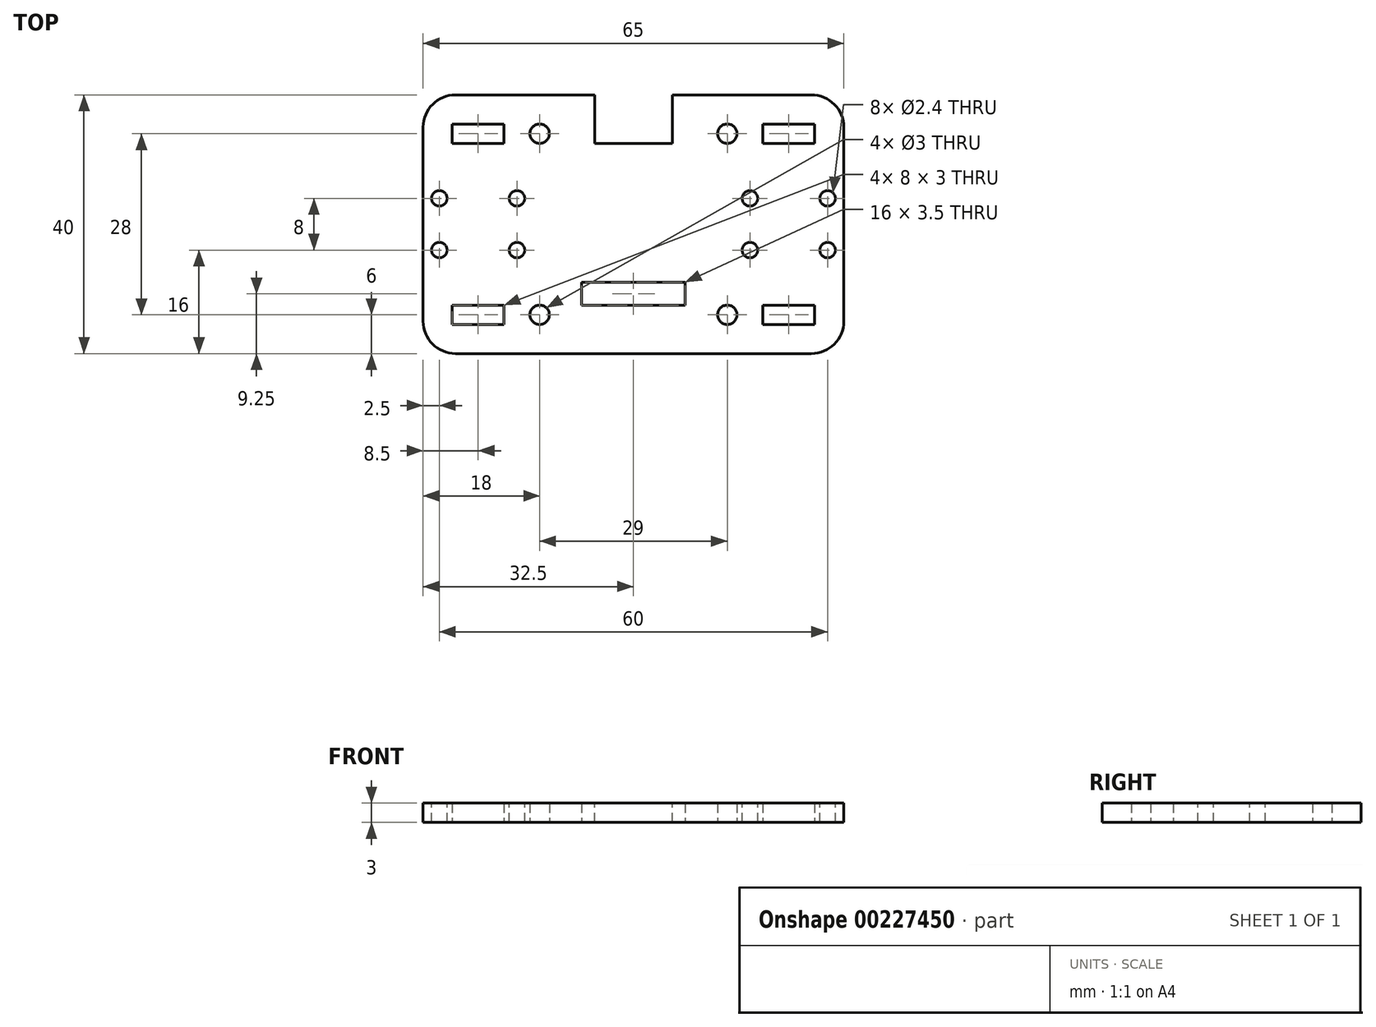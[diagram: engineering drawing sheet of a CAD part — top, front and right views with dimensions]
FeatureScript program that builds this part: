
annotation { "Feature Type Name" : "Feature", "Feature Type Description" : "" }
export const myFeature = defineFeature(function(context is Context, id is Id, definition is map)
    precondition{}
    {
        {
            assignVariable(context, id + "F0", {"name" : "Thickness", "anyValue" : 3});
        }
        {
            var Q0;
            Q0=qCreatedBy(makeId("Top.planeOp"),FACE);
            var sketch = newSketch(context, id + "F1", { "sketchPlane" : qUnion([Q0])});
            skLineSegment(sketch, "E0.bottom", {"start": v(32.5, -20) * mm, "end": v(-32.5, -20) * mm});
            skLineSegment(sketch, "E0.top", {"start": v(32.5, 20) * mm, "end": v(-32.5, 20) * mm});
            skLineSegment(sketch, "E0.left", {"start": v(32.5, -20) * mm, "end": v(32.5, 20) * mm});
            skLineSegment(sketch, "E0.right", {"start": v(-32.5, -20) * mm, "end": v(-32.5, 20) * mm});
            skPoint(sketch, "E0.middle", {"position": v(0, 0) * mm});
            skLineSegment(sketch, "E1", {"start": v(-32.5, -14) * mm, "end": v(32.5, -14) * mm, "construction": true});
            skPoint(sketch, "E2", {"position": v(-24, -14) * mm});
            skLineSegment(sketch, "E3.bottom", {"start": v(-20, -15.5) * mm, "end": v(-28, -15.5) * mm});
            skLineSegment(sketch, "E3.top", {"start": v(-20, -12.5) * mm, "end": v(-28, -12.5) * mm});
            skLineSegment(sketch, "E3.left", {"start": v(-20, -15.5) * mm, "end": v(-20, -12.5) * mm});
            skLineSegment(sketch, "E3.right", {"start": v(-28, -15.5) * mm, "end": v(-28, -12.5) * mm});
            skPoint(sketch, "E4.MirrorP", {"position": v(24, -14) * mm});
            skLineSegment(sketch, "E5.MirrorCS", {"start": v(28, -15.5) * mm, "end": v(28, -12.5) * mm});
            skLineSegment(sketch, "E6.MirrorCS", {"start": v(20, -15.5) * mm, "end": v(20, -12.5) * mm});
            skLineSegment(sketch, "E7.MirrorCS", {"start": v(20, -12.5) * mm, "end": v(28, -12.5) * mm});
            skLineSegment(sketch, "E8.MirrorCS", {"start": v(20, -15.5) * mm, "end": v(28, -15.5) * mm});
            skPoint(sketch, "E9.MirrorP", {"position": v(24, 14) * mm});
            skPoint(sketch, "E10.MirrorP", {"position": v(-24, 14) * mm});
            skLineSegment(sketch, "E11.MirrorCS", {"start": v(-20, 12.5) * mm, "end": v(-28, 12.5) * mm});
            skLineSegment(sketch, "E12.MirrorCS", {"start": v(-20, 15.5) * mm, "end": v(-20, 12.5) * mm});
            skLineSegment(sketch, "E13.MirrorCS", {"start": v(-28, 15.5) * mm, "end": v(-28, 12.5) * mm});
            skLineSegment(sketch, "E14.MirrorCS", {"start": v(28, 15.5) * mm, "end": v(28, 12.5) * mm});
            skLineSegment(sketch, "E15.MirrorCS", {"start": v(-20, 15.5) * mm, "end": v(-28, 15.5) * mm});
            skLineSegment(sketch, "E16.MirrorCS", {"start": v(20, 15.5) * mm, "end": v(28, 15.5) * mm});
            skLineSegment(sketch, "E17.MirrorCS", {"start": v(20, 15.5) * mm, "end": v(20, 12.5) * mm});
            skLineSegment(sketch, "E18.MirrorCS", {"start": v(20, 12.5) * mm, "end": v(28, 12.5) * mm});
            skCircle(sketch, "E19", {"center": v(-14.5, -14) * mm, "radius": 1.5 * mm});
            skCircle(sketch, "E20.MirrorC", {"center": v(14.5, -14) * mm, "radius": 1.5 * mm});
            skCircle(sketch, "E21.MirrorC", {"center": v(-14.5, 14) * mm, "radius": 1.5 * mm});
            skCircle(sketch, "E22.MirrorC", {"center": v(14.5, 14) * mm, "radius": 1.5 * mm});
            skLineSegment(sketch, "E23.bottom", {"start": v(-8, -12.5) * mm, "end": v(8, -12.5) * mm});
            skLineSegment(sketch, "E23.top", {"start": v(-8, -9) * mm, "end": v(8, -9) * mm});
            skLineSegment(sketch, "E23.left", {"start": v(-8, -12.5) * mm, "end": v(-8, -9) * mm});
            skLineSegment(sketch, "E23.right", {"start": v(8, -12.5) * mm, "end": v(8, -9) * mm});
            skPoint(sketch, "E24", {"position": v(0, -9) * mm});
            skSolve(sketch);
        }
        {
            var Q0;
            Q0=makeQuery(id+"F1.imprint","IMPRINT",FACE,{"disambiguationData":[TD([[makeQuery(id+"F1.imprint","IMPRINT",EDGE,{"derivedFrom":sQuery(id+"F1.wireOp",EDGE,"E0.bottom")}),-1.0]])]});
            extrude(context, id + "F2", {"entities" : qUnion([Q0]), "depth" : (getVariable(context, 'Thickness')) * mm});
        }
        {
            var Q0;
            Q0=makeQuery(id+"F2.opExtrude","CAP_FACE",FACE,{"disambiguationData":[OSD([sQuery(id+"F1.wireOp",EDGE,"E0.bottom"),sQuery(id+"F1.wireOp",EDGE,"E0.top"),sQuery(id+"F1.wireOp",EDGE,"E0.left"),sQuery(id+"F1.wireOp",EDGE,"E0.right"),sQuery(id+"F1.wireOp",EDGE,"E3.bottom"),sQuery(id+"F1.wireOp",EDGE,"E3.top"),sQuery(id+"F1.wireOp",EDGE,"E3.left"),sQuery(id+"F1.wireOp",EDGE,"E3.right"),sQuery(id+"F1.wireOp",EDGE,"E5.MirrorCS"),sQuery(id+"F1.wireOp",EDGE,"E6.MirrorCS"),sQuery(id+"F1.wireOp",EDGE,"E7.MirrorCS"),sQuery(id+"F1.wireOp",EDGE,"E8.MirrorCS"),sQuery(id+"F1.wireOp",EDGE,"E11.MirrorCS"),sQuery(id+"F1.wireOp",EDGE,"E12.MirrorCS"),sQuery(id+"F1.wireOp",EDGE,"E13.MirrorCS"),sQuery(id+"F1.wireOp",EDGE,"E14.MirrorCS"),sQuery(id+"F1.wireOp",EDGE,"E15.MirrorCS"),sQuery(id+"F1.wireOp",EDGE,"E16.MirrorCS"),sQuery(id+"F1.wireOp",EDGE,"E17.MirrorCS"),sQuery(id+"F1.wireOp",EDGE,"E18.MirrorCS"),sQuery(id+"F1.wireOp",EDGE,"E19"),sQuery(id+"F1.wireOp",EDGE,"E20.MirrorC"),sQuery(id+"F1.wireOp",EDGE,"E21.MirrorC"),sQuery(id+"F1.wireOp",EDGE,"E22.MirrorC")])],"isStart":false});
            var sketch = newSketch(context, id + "F3", { "sketchPlane" : qUnion([Q0])});
            skPoint(sketch, "E25", {"position": v(-30, 4) * mm});
            skPoint(sketch, "E26.0.1.0", {"position": v(-30, -4) * mm});
            skPoint(sketch, "E26.1.0.0", {"position": v(-18, 4) * mm});
            skPoint(sketch, "E26.1.1.0", {"position": v(-18, -4) * mm});
            skLineSegment(sketch, "E26.direction1", {"start": v(-30, 4) * mm, "end": v(-18, 4) * mm, "construction": true});
            skLineSegment(sketch, "E26.direction2", {"start": v(-30, 4) * mm, "end": v(-30, -4) * mm, "construction": true});
            skPoint(sketch, "E27.MirrorP", {"position": v(18, -4) * mm});
            skLineSegment(sketch, "E28.MirrorCS", {"start": v(30, 4) * mm, "end": v(18, 4) * mm, "construction": true});
            skLineSegment(sketch, "E29.MirrorCS", {"start": v(30, 4) * mm, "end": v(30, -4) * mm, "construction": true});
            skPoint(sketch, "E30.MirrorP", {"position": v(18, 4) * mm});
            skSolve(sketch);
        }
        {
            var Q0;
            Q0=sQuery(id+"F3.wireOp",VERTEX,"E25");
            var Q1;
            Q1=sQuery(id+"F3.wireOp",VERTEX,"E26.0.1.0");
            var Q2;
            Q2=sQuery(id+"F3.wireOp",VERTEX,"E26.1.0.0");
            var Q3;
            Q3=sQuery(id+"F3.wireOp",VERTEX,"E26.1.1.0");
            var Q4;
            Q4=sQuery(id+"F3.wireOp",VERTEX,"E30.MirrorP");
            var Q5;
            Q5=sQuery(id+"F3.wireOp",VERTEX,"E27.MirrorP");
            var Q6;
            Q6=sQuery(id+"F3.wireOp",VERTEX,"E29.MirrorCS.start");
            var Q7;
            Q7=sQuery(id+"F3.wireOp",VERTEX,"E29.MirrorCS.end");
            var Q8;
            Q8=makeQuery(id+"F2.opExtrude","SWEPT_BODY",BODY,{"disambiguationData":[OSD([sQuery(id+"F1.wireOp",EDGE,"E0.bottom"),sQuery(id+"F1.wireOp",EDGE,"E0.top"),sQuery(id+"F1.wireOp",EDGE,"E0.left"),sQuery(id+"F1.wireOp",EDGE,"E0.right"),sQuery(id+"F1.wireOp",EDGE,"E3.bottom"),sQuery(id+"F1.wireOp",EDGE,"E3.top"),sQuery(id+"F1.wireOp",EDGE,"E3.left"),sQuery(id+"F1.wireOp",EDGE,"E3.right"),sQuery(id+"F1.wireOp",EDGE,"E5.MirrorCS"),sQuery(id+"F1.wireOp",EDGE,"E6.MirrorCS"),sQuery(id+"F1.wireOp",EDGE,"E7.MirrorCS"),sQuery(id+"F1.wireOp",EDGE,"E8.MirrorCS"),sQuery(id+"F1.wireOp",EDGE,"E11.MirrorCS"),sQuery(id+"F1.wireOp",EDGE,"E12.MirrorCS"),sQuery(id+"F1.wireOp",EDGE,"E13.MirrorCS"),sQuery(id+"F1.wireOp",EDGE,"E14.MirrorCS"),sQuery(id+"F1.wireOp",EDGE,"E15.MirrorCS"),sQuery(id+"F1.wireOp",EDGE,"E16.MirrorCS"),sQuery(id+"F1.wireOp",EDGE,"E17.MirrorCS"),sQuery(id+"F1.wireOp",EDGE,"E18.MirrorCS"),sQuery(id+"F1.wireOp",EDGE,"E19"),sQuery(id+"F1.wireOp",EDGE,"E20.MirrorC"),sQuery(id+"F1.wireOp",EDGE,"E21.MirrorC"),sQuery(id+"F1.wireOp",EDGE,"E22.MirrorC")])]});
            hole(context, id + "F4", {"style" : HoleStyle.SIMPLE, "endStyle" : HoleEndStyle.THROUGH, "holeDiameter" : 2.4 * mm, "tappedDepth" : 12 * mm, "tapClearance" : 3, "locations" : qUnion([Q0, Q1, Q2, Q3, Q4, Q5, Q6, Q7]), "scope" : qUnion([Q8])});
        }
        {
            var Q0;
            Q0=makeQuery(id+"F2.opExtrude","CAP_FACE",FACE,{"disambiguationData":[OSD([sQuery(id+"F1.wireOp",EDGE,"E0.bottom"),sQuery(id+"F1.wireOp",EDGE,"E0.top"),sQuery(id+"F1.wireOp",EDGE,"E0.left"),sQuery(id+"F1.wireOp",EDGE,"E0.right"),sQuery(id+"F1.wireOp",EDGE,"E3.bottom"),sQuery(id+"F1.wireOp",EDGE,"E3.top"),sQuery(id+"F1.wireOp",EDGE,"E3.left"),sQuery(id+"F1.wireOp",EDGE,"E3.right"),sQuery(id+"F1.wireOp",EDGE,"E5.MirrorCS"),sQuery(id+"F1.wireOp",EDGE,"E6.MirrorCS"),sQuery(id+"F1.wireOp",EDGE,"E7.MirrorCS"),sQuery(id+"F1.wireOp",EDGE,"E8.MirrorCS"),sQuery(id+"F1.wireOp",EDGE,"E11.MirrorCS"),sQuery(id+"F1.wireOp",EDGE,"E12.MirrorCS"),sQuery(id+"F1.wireOp",EDGE,"E13.MirrorCS"),sQuery(id+"F1.wireOp",EDGE,"E14.MirrorCS"),sQuery(id+"F1.wireOp",EDGE,"E15.MirrorCS"),sQuery(id+"F1.wireOp",EDGE,"E16.MirrorCS"),sQuery(id+"F1.wireOp",EDGE,"E17.MirrorCS"),sQuery(id+"F1.wireOp",EDGE,"E18.MirrorCS"),sQuery(id+"F1.wireOp",EDGE,"E19"),sQuery(id+"F1.wireOp",EDGE,"E20.MirrorC"),sQuery(id+"F1.wireOp",EDGE,"E21.MirrorC"),sQuery(id+"F1.wireOp",EDGE,"E22.MirrorC"),sQuery(id+"F1.wireOp",EDGE,"E23.bottom"),sQuery(id+"F1.wireOp",EDGE,"E23.top"),sQuery(id+"F1.wireOp",EDGE,"E23.left"),sQuery(id+"F1.wireOp",EDGE,"E23.right")])],"isStart":false});
            var sketch = newSketch(context, id + "F5", { "sketchPlane" : qUnion([Q0])});
            skLineSegment(sketch, "E31.bottom", {"start": v(6, 20) * mm, "end": v(-6, 20) * mm});
            skLineSegment(sketch, "E31.top", {"start": v(6, 12.5) * mm, "end": v(-6, 12.5) * mm});
            skLineSegment(sketch, "E31.left", {"start": v(6, 20) * mm, "end": v(6, 12.5) * mm});
            skLineSegment(sketch, "E31.right", {"start": v(-6, 20) * mm, "end": v(-6, 12.5) * mm});
            skPoint(sketch, "E31.middle", {"position": v(0, 16.25) * mm});
            skSolve(sketch);
        }
        {
            var Q0;
            Q0=makeQuery(id+"F5.imprint","IMPRINT",FACE,{"disambiguationData":[TD([[makeQuery(id+"F5.imprint","IMPRINT",EDGE,{"derivedFrom":sQuery(id+"F5.wireOp",EDGE,"E31.bottom")}),1.0]])]});
            extrude(context, id + "F6", {"entities" : qUnion([Q0]), "operationType" : NewBodyOperationType.REMOVE, "oppositeDirection" : true, "depth" : 25 * mm, "offsetDistance" : 25 * mm});
        }
        {
            var Q0;
            Q0=makeQuery(id+"F2.opExtrude","SWEPT_EDGE",EDGE,{"disambiguationData":[OSD([sQuery(id+"F1.wireOp",EDGE,"E0.bottom"),sQuery(id+"F1.wireOp",EDGE,"E0.right")])]});
            var Q1;
            Q1=makeQuery(id+"F2.opExtrude","SWEPT_EDGE",EDGE,{"disambiguationData":[OSD([sQuery(id+"F1.wireOp",EDGE,"E0.top"),sQuery(id+"F1.wireOp",EDGE,"E0.right")])]});
            var Q2;
            Q2=makeQuery(id+"F2.opExtrude","SWEPT_EDGE",EDGE,{"disambiguationData":[OSD([sQuery(id+"F1.wireOp",EDGE,"E0.bottom"),sQuery(id+"F1.wireOp",EDGE,"E0.left")])]});
            var Q3;
            Q3=makeQuery(id+"F2.opExtrude","SWEPT_EDGE",EDGE,{"disambiguationData":[OSD([sQuery(id+"F1.wireOp",EDGE,"E0.top"),sQuery(id+"F1.wireOp",EDGE,"E0.left")])]});
            var Q4;
            Q4=makeQuery(id+"F6.boolean.opBoolean","COPY",EDGE,{"derivedFrom":makeQuery(id+"F6.opExtrude","SWEPT_EDGE",EDGE,{"disambiguationData":[OSD([sQuery(id+"F1.wireOp",EDGE,"E0.top"),sQuery(id+"F5.wireOp",EDGE,"E31.bottom"),sQuery(id+"F5.wireOp",EDGE,"E31.right")])]})});
            var Q5;
            Q5=makeQuery(id+"F6.boolean.opBoolean","COPY",EDGE,{"derivedFrom":makeQuery(id+"F6.opExtrude","SWEPT_EDGE",EDGE,{"disambiguationData":[OSD([sQuery(id+"F1.wireOp",EDGE,"E0.top"),sQuery(id+"F5.wireOp",EDGE,"E31.bottom"),sQuery(id+"F5.wireOp",EDGE,"E31.left")])]})});
            fillet(context, id + "F7", {"entities" : qUnion([Q0, Q1, Q2, Q3, Q4, Q5]), "radius" : 5 * mm, "tangentPropagation" : true, "allowEdgeOverflow" : false});
        }
    });
